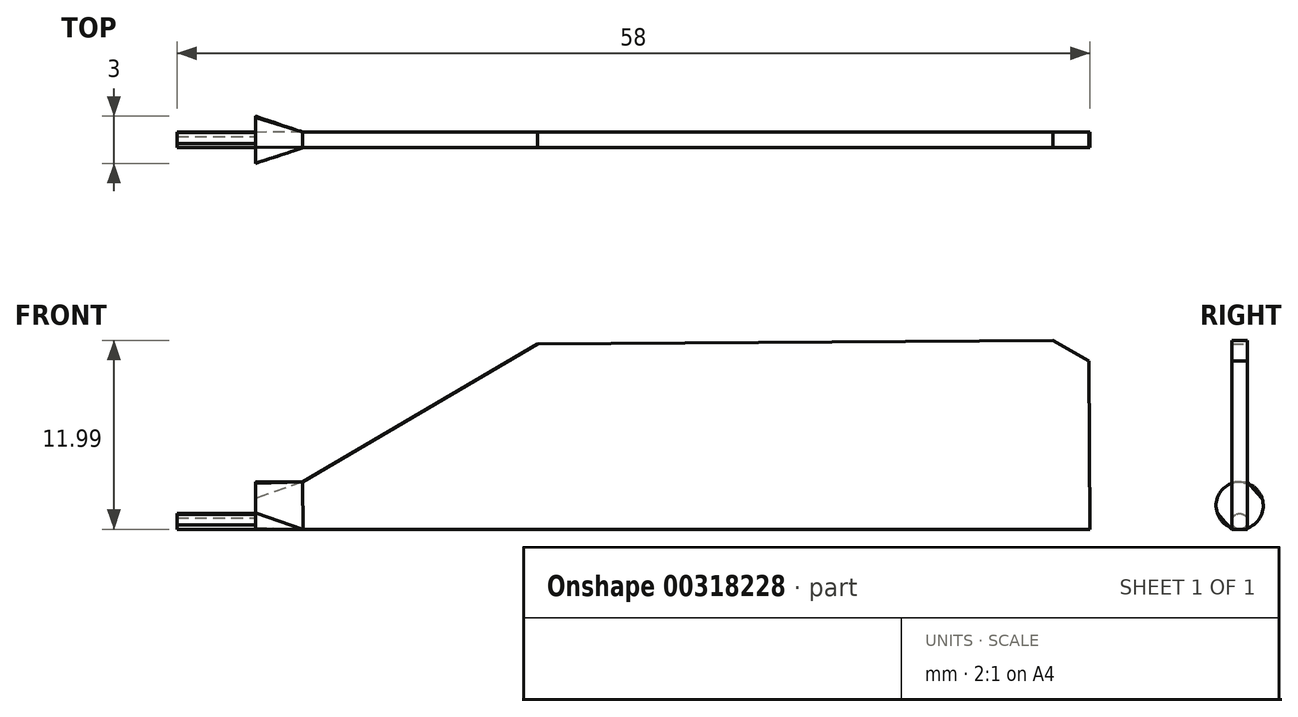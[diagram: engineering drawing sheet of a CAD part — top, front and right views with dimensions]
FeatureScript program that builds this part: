
annotation { "Feature Type Name" : "Feature", "Feature Type Description" : "" }
export const myFeature = defineFeature(function(context is Context, id is Id, definition is map)
    precondition{}
    {
        {
            var Q0;
            Q0=qCreatedBy(makeId("Front.planeOp"),FACE);
            var sketch = newSketch(context, id + "F0", { "sketchPlane" : qUnion([Q0])});
            skLineSegment(sketch, "E0.bottom", {"start": v(0, 0) * mm, "end": v(50, 0) * mm});
            skLineSegment(sketch, "E0.left", {"start": v(0, 0) * mm, "end": v(-0.03, 3) * mm});
            skLineSegment(sketch, "E0.right", {"start": v(50, 0) * mm, "end": v(49.9, 12) * mm});
            skLineSegment(sketch, "E1", {"start": v(14.9, 11.79) * mm, "end": v(-0.03, 3) * mm});
            skPoint(sketch, "E2.orphan", {"position": v(-0.05, 6) * mm});
            skLineSegment(sketch, "E3", {"start": v(14.9, 11.79) * mm, "end": v(49.9, 12) * mm});
            skSolve(sketch);
        }
        {
            var Q0;
            Q0 = qSketchRegion(id + "F0", true);
            extrude(context, id + "F1", {"entities" : qUnion([Q0]), "endBound" : BoundingType.SYMMETRIC, "depth" : 1 * mm});
        }
        {
            var Q0;
            Q0=qCreatedBy(makeId("Right.planeOp"),FACE);
            cPlane(context, id + "F2", {"entities" : qUnion([Q0]), "cplaneType" : CPlaneType.OFFSET, "offset" : 3 * mm, "oppositeDirection" : true, "width" : 150 * mm, "height" : 150 * mm});
        }
        {
            var Q0;
            Q0=qCreatedBy(id+"F2.planeOp",FACE);
            var sketch = newSketch(context, id + "F3", { "sketchPlane" : qUnion([Q0])});
            skCircle(sketch, "E4", {"center": v(0, 1.5) * mm, "radius": 1.5 * mm});
            skPoint(sketch, "E5.0", {"position": v(0, 0) * mm});
            skSolve(sketch);
        }
        {
            var Q1;
            Q1=makeQuery(id+"F1.opExtrude","SWEPT_FACE",FACE,{"disambiguationData":[OSD([sQuery(id+"F0.wireOp",EDGE,"E0.left")])]});
            var Q2;
            Q2=makeQuery(id+"F3.imprint","IMPRINT",FACE,{"disambiguationData":[TD([[makeQuery(id+"F3.imprint","IMPRINT",EDGE,{"derivedFrom":sQuery(id+"F3.wireOp",EDGE,"E4")}),1.0]])]});
            loft(context, id + "F4", {"operationType" : NewBodyOperationType.ADD, "sheetProfilesArray" : [{ "sheetProfileEntities" : qUnion([Q1]) }, { "sheetProfileEntities" : qUnion([Q2]) }]});
        }
        {
            var Q0;
            Q0=makeQuery(id+"F4.opLoft","CAP_FACE",FACE,{"disambiguationData":[OSD([makeQuery(id+"F3.imprint","IMPRINT",FACE,{"disambiguationData":[TD([[makeQuery(id+"F3.imprint","IMPRINT",EDGE,{"derivedFrom":sQuery(id+"F3.wireOp",EDGE,"E4")}),1.0]])]})])],"isStart":true});
            var sketch = newSketch(context, id + "F5", { "sketchPlane" : qUnion([Q0])});
            skFitSpline(sketch, "E6.0.0", {"points": [v(-0.45, 0.72) * mm, v(-0.48, 0.66) * mm, v(-0.5, 0.6) * mm, v(-0.5, 0.54) * mm, v(-0.5, 0.47) * mm, v(-0.5, 0.4) * mm, v(-0.47, 0.34) * mm, v(-0.45, 0.28) * mm, v(-0.42, 0.22) * mm, v(-0.38, 0.17) * mm, v(-0.33, 0.12) * mm, v(-0.28, 0.08) * mm, v(-0.22, 0.05) * mm]});
            skFitSpline(sketch, "E6.0.1", {"points": [v(-0.22, 0.05) * mm, v(-0.16, 0.02) * mm, v(-0.1, 0) * mm, v(-0.04, 0) * mm, v(0.03, 0) * mm, v(0.1, 0) * mm, v(0.16, 0.03) * mm, v(0.22, 0.05) * mm, v(0.28, 0.08) * mm, v(0.33, 0.12) * mm, v(0.38, 0.17) * mm, v(0.42, 0.22) * mm, v(0.45, 0.28) * mm]});
            skFitSpline(sketch, "E6.0.2", {"points": [v(0.45, 0.28) * mm, v(0.48, 0.34) * mm, v(0.5, 0.4) * mm, v(0.5, 0.46) * mm, v(0.5, 0.53) * mm, v(0.5, 0.6) * mm, v(0.47, 0.66) * mm, v(0.45, 0.72) * mm, v(0.42, 0.78) * mm, v(0.38, 0.83) * mm, v(0.33, 0.88) * mm, v(0.28, 0.92) * mm, v(0.22, 0.95) * mm]});
            skFitSpline(sketch, "E6.0.3", {"points": [v(0.22, 0.95) * mm, v(0.16, 0.98) * mm, v(0.1, 1) * mm, v(0.04, 1) * mm, v(-0.03, 1) * mm, v(-0.1, 1) * mm, v(-0.16, 0.97) * mm, v(-0.22, 0.95) * mm, v(-0.28, 0.92) * mm, v(-0.33, 0.88) * mm, v(-0.38, 0.83) * mm, v(-0.42, 0.78) * mm, v(-0.45, 0.72) * mm]});
            skFitSpline(sketch, "E7.0.0", {"points": [v(-0.45, 0.72) * mm, v(-0.48, 0.66) * mm, v(-0.5, 0.6) * mm, v(-0.5, 0.54) * mm, v(-0.5, 0.47) * mm, v(-0.5, 0.4) * mm, v(-0.47, 0.34) * mm, v(-0.45, 0.28) * mm, v(-0.42, 0.22) * mm, v(-0.38, 0.17) * mm, v(-0.33, 0.12) * mm, v(-0.28, 0.08) * mm, v(-0.22, 0.05) * mm]});
            skFitSpline(sketch, "E7.0.1", {"points": [v(-0.22, 0.05) * mm, v(-0.16, 0.02) * mm, v(-0.1, 0) * mm, v(-0.04, 0) * mm, v(0.03, 0) * mm, v(0.1, 0) * mm, v(0.16, 0.03) * mm, v(0.22, 0.05) * mm, v(0.28, 0.08) * mm, v(0.33, 0.12) * mm, v(0.38, 0.17) * mm, v(0.42, 0.22) * mm, v(0.45, 0.28) * mm]});
            skFitSpline(sketch, "E7.0.2", {"points": [v(0.45, 0.28) * mm, v(0.48, 0.34) * mm, v(0.5, 0.4) * mm, v(0.5, 0.46) * mm, v(0.5, 0.53) * mm, v(0.5, 0.6) * mm, v(0.47, 0.66) * mm, v(0.45, 0.72) * mm, v(0.42, 0.78) * mm, v(0.38, 0.83) * mm, v(0.33, 0.88) * mm, v(0.28, 0.92) * mm, v(0.22, 0.95) * mm]});
            skFitSpline(sketch, "E7.0.3", {"points": [v(0.22, 0.95) * mm, v(0.16, 0.98) * mm, v(0.1, 1) * mm, v(0.04, 1) * mm, v(-0.03, 1) * mm, v(-0.1, 1) * mm, v(-0.16, 0.97) * mm, v(-0.22, 0.95) * mm, v(-0.28, 0.92) * mm, v(-0.33, 0.88) * mm, v(-0.38, 0.83) * mm, v(-0.42, 0.78) * mm, v(-0.45, 0.72) * mm]});
            skSolve(sketch);
        }
        {
            var Q0;
            Q0 = qSketchRegion(id + "F5", true);
            extrude(context, id + "F6", {"entities" : qUnion([Q0]), "operationType" : NewBodyOperationType.ADD, "depth" : 5 * mm});
        }
        {
            var Q0;
            Q0=makeQuery(id+"F1.opExtrude","CAP_FACE",FACE,{"disambiguationData":[OSD([sQuery(id+"F0.wireOp",EDGE,"E0.bottom"),sQuery(id+"F0.wireOp",EDGE,"E0.left"),sQuery(id+"F0.wireOp",EDGE,"E0.right"),sQuery(id+"F0.wireOp",EDGE,"E1"),sQuery(id+"F0.wireOp",EDGE,"E3")])],"isStart":false});
            var sketch = newSketch(context, id + "F7", { "sketchPlane" : qUnion([Q0])});
            skLineSegment(sketch, "E8", {"start": v(47.64, 11.99) * mm, "end": v(49.9, 10.7) * mm});
            skLineSegment(sketch, "E9.0", {"start": v(47.64, 11.99) * mm, "end": v(49.9, 12) * mm});
            skLineSegment(sketch, "E10.0", {"start": v(49.9, 10.7) * mm, "end": v(49.9, 12) * mm});
            skPoint(sketch, "E11.orphan", {"position": v(14.9, 11.79) * mm});
            skPoint(sketch, "E12.orphan", {"position": v(50, 0) * mm});
            skSolve(sketch);
        }
        {
            var Q0;
            Q0 = qSketchRegion(id + "F7", true);
            extrude(context, id + "F8", {"entities" : qUnion([Q0]), "operationType" : NewBodyOperationType.REMOVE, "oppositeDirection" : true, "depth" : 25 * mm});
        }
    });
